# Revit family: Korobka soedinitelnaya dlya greyushchego kabelya KSGK-2 AYaKS
name_source: partatom
category: Датчики
units: mm (PartAtom-declared; Revit-internal decimal feet)

## family parameters
Всегда вертикально = Да
Заголовок OmniClass = Communication and Data Processing Equipment
На основе рабочей плоскости = Нет
Номер OmniClass = 23.85.50.17
Общий = Нет
При загрузке вырезать с полостями = Нет
Размер круглого соединителя = Использовать диаметр
Сохранять ориентацию аннотаций = Нет
Тип детали = Нормальный
Точка принадлежности помещению = Нет

## types (1)
- КСГК-2
    ADSK_Единица измерения = шт.
    ADSK_Завод-изготовитель = ООО НПП «МАГНИТО-КОНТАКТ»
    ADSK_Масса = 1.3
    ADSK_Материал = Пластик белый
    ADSK_Наименование = Коробка соединительная для греющего кабеля КСГК IP66 АЯКС
    ADSK_Наименование краткое = КСГК-2
    ADSK_Обозначение = АТФЕ.685552.234 ПС
    ADSK_Размер_Высота = 93 мм
    ADSK_Размер_Длина = 370 мм
    ADSK_Размер_Ширина = 150 мм
    URL = https://m-kontakt.ru
    Диапазон рабочих температур, °C = от -65 до +70
    Изготовитель = ООО НПП «МАГНИТО-КОНТАКТ»
    Кол-во клеммных пар (из них пар заземления), шт = 12(2)
    Напряжение, В = не более 600
    Описание = Коробка соединительная для греющего кабеля КСГК IP66 АЯКС (далее – коробка) предназначена для подключения питающего кабеля к сети нагревательных кабелей, сращивания отрезков греющего кабеля или разветвления греющих кабелей в цепях переменного и постоянного тока. Внутри коробок располагаются пружинные клеммные колодки 10мм2.
    Отметка по умолчанию = 0 мм
    Степень защиты оболочки = IP 66 по ГОСТ 14254-2015
    Ток, А = не более 70
